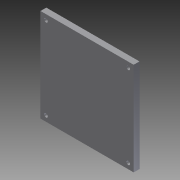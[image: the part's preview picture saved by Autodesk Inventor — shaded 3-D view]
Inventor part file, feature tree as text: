
AUTODESK INVENTOR PART (.ipt)
format: ipt  version: 2011 (Build 150239000, 239)  size: 162,304 bytes
history: native  units: in
note: dims shown in document units (in); Inventor stores cm internally (conversion verified against a paired STEP export)
features: extrude x10, sketch x10, fillet x1
ambient origin geometry x8: Origin, YZ Plane, XZ Plane, XY Plane, X Axis, Y Axis, Z Axis, Center Point
bodies: Solid1 (feature_tree)
feature tree (21):
  extrude  "Extrusion1"  Depth=4.0in
  extrude  "Extrusion2"  Depth=2.16in
  extrude  "Extrusion3"  Depth=1.7655in
  extrude  "Extrusion4"  Depth=0.029in TaperAngle=0.0deg
  extrude  "Extrusion5"  Depth=2.36in
  fillet  "Fillet1"  Radius=2.56in
  extrude  "Extrusion6"  Depth=0.125in
  extrude  "Extrusion7"  Depth=0.25in TaperAngle=0.0deg
  extrude  "Extrusion8"  Depth=0.25in
  extrude  "Extrusion9"  Depth=1.0in TaperAngle=0.0deg
  extrude  "Extrusion10"  Depth=0.25in TaperAngle=0.0deg
  sketch  "Sketch1"  dims[d0=4.0in d1=4.0in]
  sketch  "Sketch2"  dims[d2=0.029in d3=0.0in d4=2.16in]
  sketch  "Sketch3"  dims[d5=0.029in d6=0.0in d7=1.7655in]
  sketch  "Sketch4"  dims[d8=0.156in d9=0.029in d10=0.0in]
  sketch  "Sketch5"  dims[d11=0.029in d12=0.0in d13=2.36in d14=2.56in]
  sketch  "Sketch6"  dims[d15=0.262in d16=0.0in d17=0.125in]
  sketch  "Sketch7"  dims[d18=0.25in d19=0.0in d20=0.25in d21=0.0in]
  sketch  "Sketch8"  dims[d22=0.25in d23=0.25in]
  sketch  "Sketch9"  dims[d24=0.5in d25=1.0in d26=0.0in]
  sketch  "Sketch10"  dims[d27=1.0in d28=0.0in d29=0.25in d30=0.0in]
